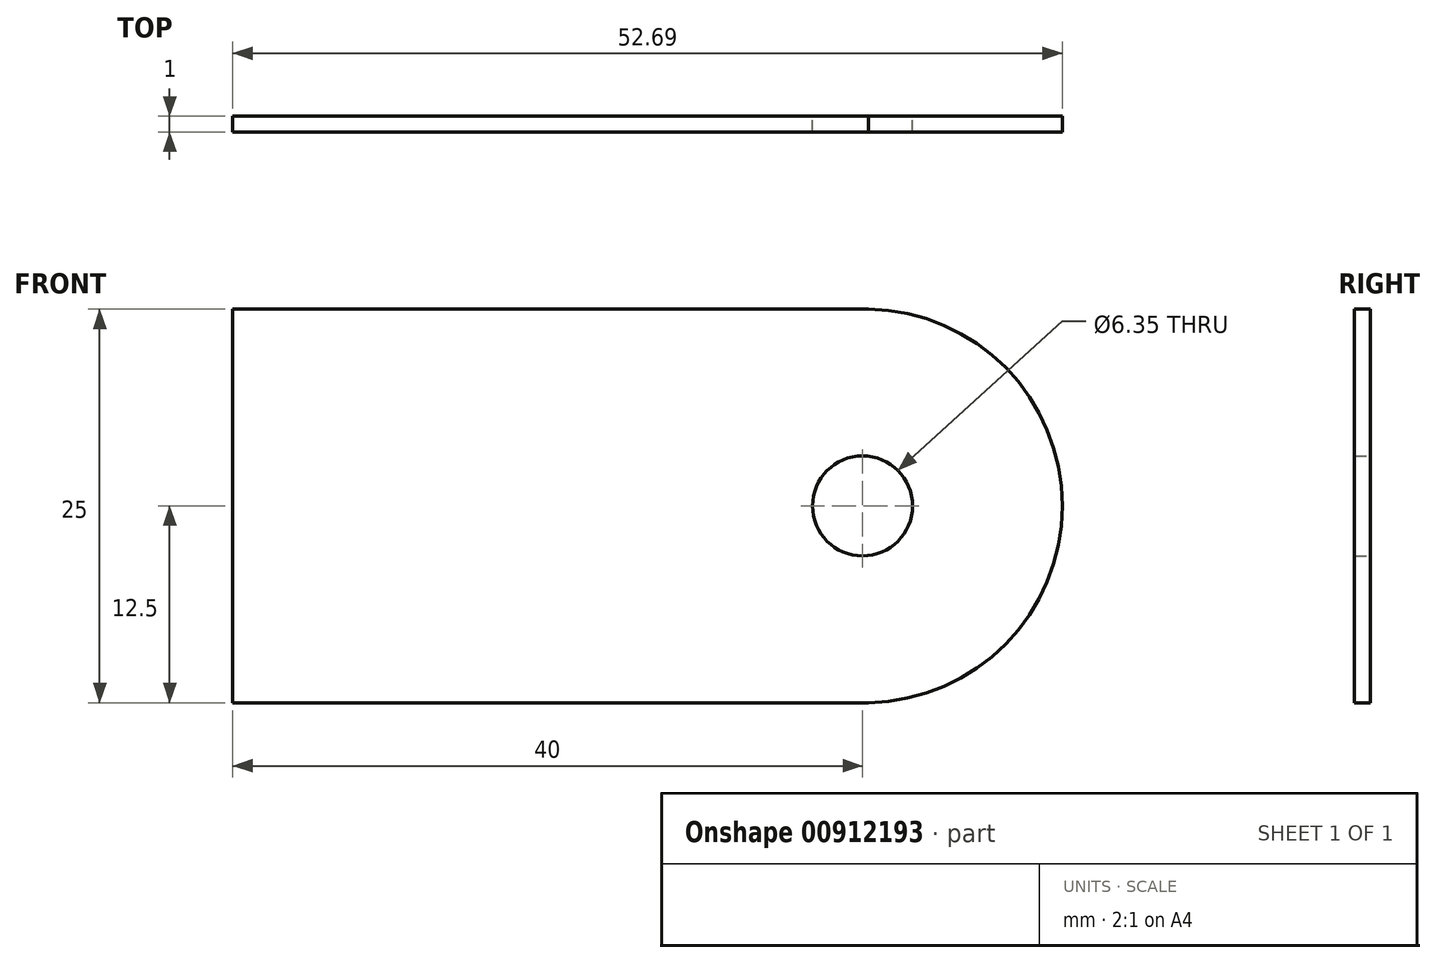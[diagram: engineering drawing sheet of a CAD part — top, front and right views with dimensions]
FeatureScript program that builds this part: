
annotation { "Feature Type Name" : "Feature", "Feature Type Description" : "" }
export const myFeature = defineFeature(function(context is Context, id is Id, definition is map)
    precondition{}
    {
        {
            var Q0;
            Q0=qCreatedBy(makeId("Front.planeOp"),FACE);
            var sketch = newSketch(context, id + "F0", { "sketchPlane" : qUnion([Q0])});
            skLineSegment(sketch, "E0.bottom", {"start": v(0, 0) * mm, "end": v(50, 0) * mm});
            skLineSegment(sketch, "E0.top", {"start": v(0, 25) * mm, "end": v(50, 25) * mm});
            skLineSegment(sketch, "E0.left", {"start": v(0, 0) * mm, "end": v(0, 25) * mm});
            skCircle(sketch, "E1", {"center": v(40, 12.5) * mm, "radius": 3.18 * mm});
            skArc(sketch, "E2", {"start": v(40, 0) * mm, "mid": v(52.7, 12.5) * mm, "end": v(40, 25) * mm});
            skSolve(sketch);
        }
        {
            var Q0;
            {var subQ0=sQuery(id+"F0.wireOp",EDGE,"E0.left");Q0=makeQuery(id+"F0.imprint","IMPRINT",FACE,{"disambiguationData":[TD([[makeQuery(id+"F0.imprint","IMPRINT",EDGE,{"derivedFrom":subQ0}),-1.0]])]});}
            extrude(context, id + "F1", {"entities" : qUnion([Q0]), "depth" : 1 * mm, "offsetDistance" : 25 * mm});
        }
    });
